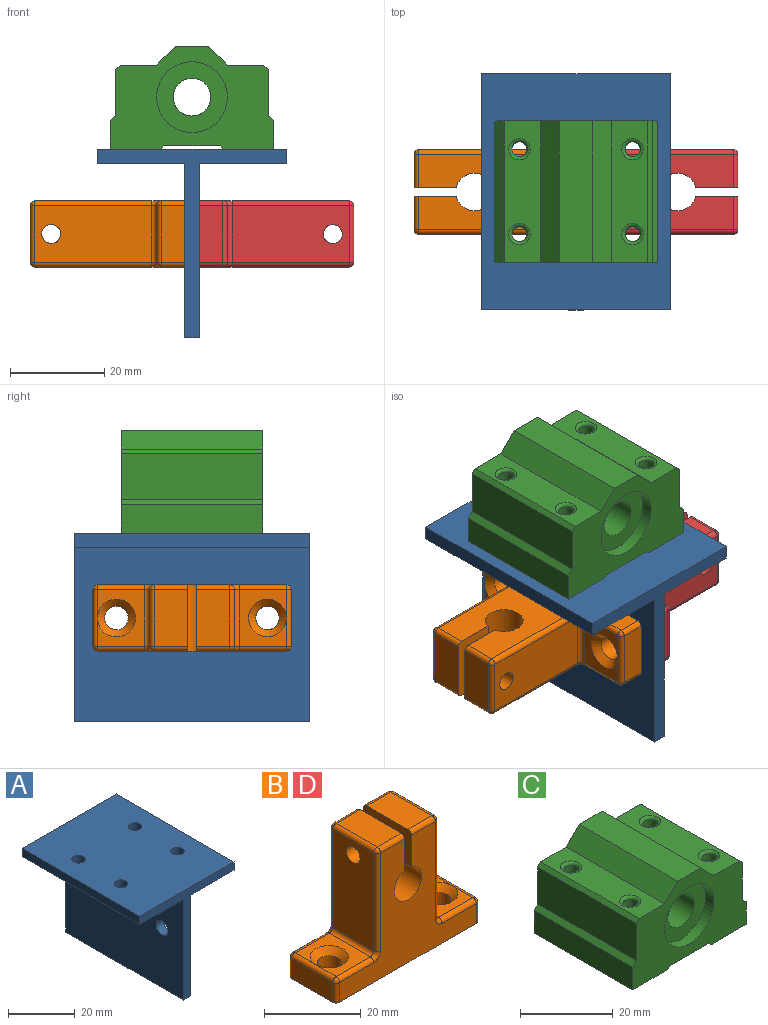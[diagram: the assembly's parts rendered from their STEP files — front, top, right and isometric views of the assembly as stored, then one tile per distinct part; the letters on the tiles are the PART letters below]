
ASSEMBLY  parts=4 mates=9
PART A: 16 faces, bbox 40x50x40 mm
  f0: plane 50x37mm, normal (-1,0,0), area 1810.7mm2, adj f4,f7,f8,f9,f14,f15
  f1: plane 50x37mm, normal (1,0,0), area 1810.7mm2, adj f3,f7,f8,f9,f14,f15
  f2: plane 50x40mm, normal (0,0,1), area 1949.7mm2, adj f5,f6,f8,f9,f10,f11,f12,f13
  f3: plane 50x18.5mm, normal (0,0,-1), area 899.9mm2, adj f1,f5,f8,f9,f12,f13
  f4: plane 50x18.5mm, normal (0,0,-1), area 899.9mm2, adj f0,f6,f8,f9,f10,f11
  f5: plane 50x3mm, normal (1,0,0), area 150mm2, adj f2,f3,f8,f9
  f6: plane 50x3mm, normal (-1,0,0), area 150mm2, adj f2,f4,f8,f9
  f7: plane 50x3mm, normal (0,0,-1), area 150mm2, adj f0,f1,f8,f9
  f8: plane 40x40mm, normal (0,-1,0), area 231mm2, adj f0,f1,f2,f3,f4,f5,f6,f7
  f9: plane 40x40mm, normal (0,1,0), area 231mm2, adj f0,f1,f2,f3,f4,f5,f6,f7
  f10: cylinder r=2mm len=4mm, axis (0,0,1), area 37.7mm2, adj f2,f4
  f11: cylinder r=2mm len=4mm, axis (0,0,1), area 37.7mm2, adj f2,f4
  f12: cylinder r=2mm len=4mm, axis (0,0,1), area 37.7mm2, adj f2,f3
  f13: cylinder r=2mm len=4mm, axis (0,0,1), area 37.7mm2, adj f2,f3
  f14: cylinder r=2.5mm len=5mm, axis (-1,0,0), area 47.1mm2, adj f0,f1
  f15: cylinder r=2.5mm len=5mm, axis (-1,0,0), area 47.1mm2, adj f0,f1
PART B: 54 faces, bbox 42x14x32.8 mm
  f0: plane 12x7mm, normal (0,0,1), area 84mm2, adj f14,f39,f47,f48
  f1: plane 12x10mm, normal (0,0,1), area 69.7mm2, adj f18,f41,f42,f49,f50
  f2: plane 12x10mm, normal (0,0,1), area 69.7mm2, adj f19,f24,f25,f32,f33
  f3: plane 42x14mm, normal (0,0,-1), area 547.9mm2, adj f4,f5,f6,f7,f8,f9,f20,f26
  f4: plane 40x31.8mm, normal (0,-1,0), area 564.6mm2, adj f3,f13,f14,f15,f20,f22,f23,f24
  f5: plane 12x5mm, normal (1,0,0), area 60mm2, adj f3,f37,f40,f41
  f6: plane 40x31.8mm, normal (0,1,0), area 564.6mm2, adj f3,f13,f14,f15,f26,f30,f33,f35
  f7: plane 12x5mm, normal (-1,0,0), area 60mm2, adj f3,f20,f25,f26
  f8: cylinder r=2.5mm len=5mm, axis (0,0,1), area 70.7mm2, adj f3,f18
  f9: cylinder r=2.5mm len=5mm, axis (0,0,1), area 70.7mm2, adj f3,f19
  f10: plane 24.8x12mm, normal (1,0,0), area 285mm2, adj f17,f43,f47,f50,f53
  f11: plane 24.8x12mm, normal (-1,0,0), area 285mm2, adj f16,f23,f31,f32,f36
  f12: plane 12x7mm, normal (0,0,1), area 84mm2, adj f15,f22,f30,f31
  f13: cylinder r=4mm len=14mm, axis (0,-1,0), area 323.6mm2, adj f4,f6,f14,f15
  f14: plane 14x8.93mm, normal (-1,0,0), area 112mm2, adj f0,f4,f6,f13,f17,f39,f48
  f15: plane 14x8.93mm, normal (1,0,0), area 112mm2, adj f4,f6,f12,f13,f16,f22,f30
  f16: cylinder r=2mm len=8mm, axis (1,0,0), area 100.5mm2, adj f11,f15
  f17: cylinder r=2mm len=8mm, axis (1,0,0), area 100.5mm2, adj f10,f14
  f18: cone r=4mm half-angle=45deg, axis (0,0,1), area 43.3mm2, adj f1,f8
  f19: cone r=2.5mm half-angle=45deg, axis (0,0,1), area 43.3mm2, adj f2,f9
  f20: cylinder r=1mm len=5mm, axis (0,0,1), area 7.9mm2, adj f3,f4,f7,f21
  f21: sphere r=1mm, area 1.6mm2, adj f20,f24,f25
  f22: cylinder r=1mm len=7mm, axis (-1,0,0), area 11mm2, adj f4,f12,f15,f27
  f23: cylinder r=1mm len=24.8mm, axis (0,0,1), area 39mm2, adj f4,f11,f27,f28
  f24: cylinder r=1mm len=10mm, axis (-1,0,0), area 15.7mm2, adj f2,f4,f21,f28
  f25: cylinder r=1mm len=12mm, axis (0,1,0), area 18.8mm2, adj f2,f7,f21,f29
  f26: cylinder r=1mm len=5mm, axis (0,0,-1), area 7.9mm2, adj f3,f6,f7,f29
  f27: sphere r=1mm, area 1.6mm2, adj f22,f23,f31
  f28: torus R=2mm, axis (0,-1,0), area 3.4mm2, adj f4,f23,f24,f32
  f29: sphere r=1mm, area 1.6mm2, adj f25,f26,f33
  f30: cylinder r=1mm len=7mm, axis (1,0,0), area 11mm2, adj f6,f12,f15,f34
  f31: cylinder r=1mm len=12mm, axis (0,1,0), area 18.8mm2, adj f11,f12,f27,f34
  f32: cylinder r=1mm len=12mm, axis (0,-1,0), area 18.8mm2, adj f2,f11,f28,f35
  f33: cylinder r=1mm len=10mm, axis (1,0,0), area 15.7mm2, adj f2,f6,f29,f35
  f34: sphere r=1mm, area 1.6mm2, adj f30,f31,f36
  f35: torus R=2mm, axis (0,-1,0), area 3.4mm2, adj f6,f32,f33,f36
  f36: cylinder r=1mm len=24.8mm, axis (0,0,-1), area 39mm2, adj f6,f11,f34,f35
  f37: cylinder r=1mm len=5mm, axis (0,0,-1), area 7.9mm2, adj f3,f4,f5,f38
  f38: sphere r=1mm, area 1.6mm2, adj f37,f41,f42
  f39: cylinder r=1mm len=7mm, axis (-1,0,0), area 11mm2, adj f0,f4,f14,f44
  f40: cylinder r=1mm len=5mm, axis (0,0,1), area 7.9mm2, adj f3,f5,f6,f45
  f41: cylinder r=1mm len=12mm, axis (0,-1,0), area 18.8mm2, adj f1,f5,f38,f45
  f42: cylinder r=1mm len=10mm, axis (-1,0,0), area 15.7mm2, adj f1,f4,f38,f46
  f43: cylinder r=1mm len=24.8mm, axis (0,0,-1), area 39mm2, adj f4,f10,f44,f46
  f44: sphere r=1mm, area 1.6mm2, adj f39,f43,f47
  f45: sphere r=1mm, area 1.6mm2, adj f40,f41,f49
  f46: torus R=2mm, axis (0,-1,0), area 3.4mm2, adj f4,f42,f43,f50
  f47: cylinder r=1mm len=12mm, axis (0,-1,0), area 18.8mm2, adj f0,f10,f44,f51
  f48: cylinder r=1mm len=7mm, axis (1,0,0), area 11mm2, adj f0,f6,f14,f51
  f49: cylinder r=1mm len=10mm, axis (1,0,0), area 15.7mm2, adj f1,f6,f45,f52
  f50: cylinder r=1mm len=12mm, axis (0,1,0), area 18.8mm2, adj f1,f10,f46,f52
  f51: sphere r=1mm, area 1.6mm2, adj f47,f48,f53
  f52: torus R=2mm, axis (0,-1,0), area 3.4mm2, adj f6,f49,f50,f53
  f53: cylinder r=1mm len=24.8mm, axis (0,0,1), area 39mm2, adj f6,f10,f51,f52
PART C: 37 faces, bbox 34.6x30x21.8 mm
  f0: plane 34.6x21.8mm, normal (0,1,0), area 448.1mm2, adj f1,f2,f3,f4,f5,f6,f7,f8
  f1: plane 30x7.74mm, normal (0,0,1), area 199.4mm2, adj f0,f16,f17,f32,f33,f36
  f2: plane 30x9.76mm, normal (-1,0,0), area 292.8mm2, adj f0,f3,f17,f36
  f3: plane 30x1.16mm, normal (-0.71,0,0.71), area 49.2mm2, adj f0,f2,f4,f17
  f4: plane 30x5.98mm, normal (-1,0,0), area 179.4mm2, adj f0,f3,f5,f17
  f5: plane 30x10.65mm, normal (0,0,-1), area 277.5mm2, adj f0,f4,f6,f17,f27,f29
  f6: plane 30x0.65mm, normal (0.71,0,-0.71), area 27.6mm2, adj f0,f5,f7,f17
  f7: plane 30x12mm, normal (0,0,-1), area 360mm2, adj f0,f6,f8,f17
  f8: plane 30x0.65mm, normal (-0.71,0,-0.71), area 27.6mm2, adj f0,f7,f9,f17
  f9: plane 30x10.65mm, normal (0,0,-1), area 277.5mm2, adj f0,f8,f10,f17,f28,f30
  f10: plane 30x5.98mm, normal (1,0,0), area 179.4mm2, adj f0,f9,f11,f17
  f11: plane 30x1.16mm, normal (0.71,0,0.71), area 49.2mm2, adj f0,f10,f12,f17
  f12: plane 30x9.76mm, normal (1,0,0), area 292.8mm2, adj f0,f11,f17,f35
  f13: plane 30x7.74mm, normal (0,0,1), area 199.4mm2, adj f0,f14,f17,f31,f34,f35
  f14: plane 30x4mm, normal (0.71,0,0.71), area 169.7mm2, adj f0,f13,f15,f17
  f15: plane 30x7mm, normal (0,0,1), area 210mm2, adj f0,f14,f16,f17
  f16: plane 30x4mm, normal (-0.71,0,0.71), area 169.7mm2, adj f0,f1,f15,f17
  f17: plane 34.6x21.8mm, normal (0,-1,0), area 448.1mm2, adj f1,f2,f3,f4,f5,f6,f7,f8
  f18: cylinder r=7.5mm len=15mm, axis (0,-1,0), area 117.8mm2, adj f17,f19
  f19: plane 15x15mm, normal (0,-1,0), area 126.4mm2, adj f18,f22
  f20: cylinder r=7.5mm len=15mm, axis (0,1,0), area 117.8mm2, adj f0,f21
  f21: plane 15x15mm, normal (0,1,0), area 126.4mm2, adj f20,f22
  f22: cylinder r=4mm len=25mm, axis (0,-1,0), area 628.3mm2, adj f19,f21
  f23: cylinder r=1.58mm len=16.1mm, axis (0,0,-1), area 160.3mm2, adj f29,f33
  f24: cylinder r=1.58mm len=16.1mm, axis (0,0,-1), area 160.3mm2, adj f27,f32
  f25: cylinder r=1.58mm len=16.1mm, axis (0,0,-1), area 160.3mm2, adj f28,f31
  f26: cylinder r=1.58mm len=16.1mm, axis (0,0,-1), area 160.3mm2, adj f30,f34
  f27: torus R=2.58mm, axis (0,0,1), area 19.2mm2, adj f5,f24
  f28: torus R=2.58mm, axis (0,0,1), area 19.2mm2, adj f9,f25
  f29: torus R=2.58mm, axis (0,0,1), area 19.2mm2, adj f5,f23
  f30: torus R=2.58mm, axis (0,0,1), area 19.2mm2, adj f9,f26
  f31: torus R=2.29mm, axis (0,0,-1), area 12.7mm2, adj f13,f25
  f32: torus R=2.29mm, axis (0,0,-1), area 12.7mm2, adj f1,f24
  f33: torus R=2.29mm, axis (0,0,-1), area 12.7mm2, adj f1,f23
  f34: torus R=2.29mm, axis (0,0,-1), area 12.7mm2, adj f13,f26
  f35: plane 30x0.9mm, normal (0.71,0,0.71), area 38.2mm2, adj f0,f12,f13,f17
  f36: plane 30x0.9mm, normal (-0.71,0,0.71), area 38.2mm2, adj f0,f1,f2,f17
PART D: same geometry as B
PLACE A t=(-30.62,-43.55,3.19)mm
PLACE B rot(axis=(0.58,-0.58,-0.58),120deg) t=(-32.12,-43.55,-11.81)mm
PLACE C t=(-30.62,-43.55,15.42)mm
PLACE D rot(axis=(-0.58,0.58,-0.58),120deg) t=(-29.12,-43.55,-11.81)mm
MATE planar C.f9 <-> A.f2  axis (0,0,-1) through (-18.65,-43.55,6.19)mm
MATE parallel D.f6 <-> A.f7  axis (0,0,-1) through (-16.8,-43.55,-18.81)mm
MATE parallel B.f6 <-> A.f7  axis (0,0,1) through (-44.44,-43.55,-4.81)mm
MATE parallel C.f0 <-> A.f9  axis (0,1,0) through (-30.62,-28.55,15.26)mm
MATE planar D.f3 <-> A.f1  axis (-1,0,0) through (-29.12,-43.55,-11.81)mm
MATE planar B.f3 <-> A.f0  axis (1,0,0) through (-32.12,-43.55,-11.81)mm
MATE cylindrical D.f9 <-> A.f15  axis (-1,0,0) through (-29.12,-27.55,-11.81)mm
MATE cylindrical C.f23 <-> A.f11  axis (0,0,1) through (-42.62,-52.55,7.19)mm
MATE cylindrical A.f14 <-> B.f8  axis (-1,0,0) through (-32.12,-59.55,-11.81)mm
